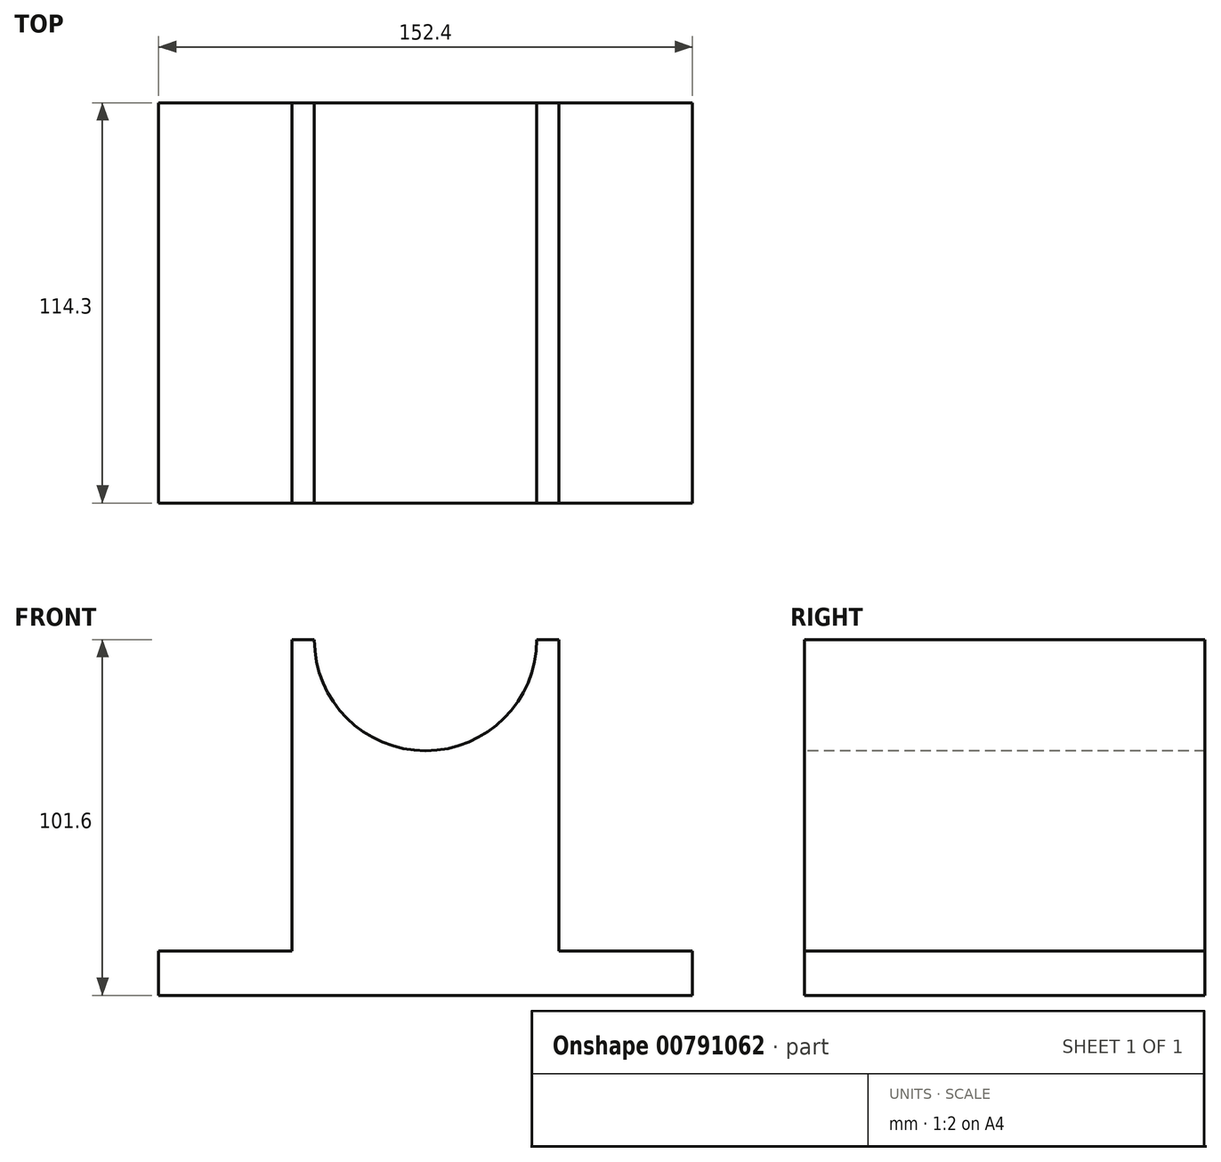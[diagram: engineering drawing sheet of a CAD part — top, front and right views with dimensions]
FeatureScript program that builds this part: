
annotation { "Feature Type Name" : "Feature", "Feature Type Description" : "" }
export const myFeature = defineFeature(function(context is Context, id is Id, definition is map)
    precondition{}
    {
        {
            var Q0;
            Q0=qCreatedBy(makeId("Front.planeOp"),FACE);
            var sketch = newSketch(context, id + "F0", { "sketchPlane" : qUnion([Q0])});
            skLineSegment(sketch, "E0", {"start": v(0, 0) * mm, "end": v(152.4, 0) * mm});
            skLineSegment(sketch, "E1", {"start": v(152.4, 0) * mm, "end": v(152.4, 12.7) * mm});
            skLineSegment(sketch, "E2", {"start": v(152.4, 12.7) * mm, "end": v(114.3, 12.7) * mm});
            skLineSegment(sketch, "E3", {"start": v(114.3, 12.7) * mm, "end": v(114.3, 101.6) * mm});
            skLineSegment(sketch, "E4", {"start": v(114.3, 101.6) * mm, "end": v(38.1, 101.6) * mm});
            skLineSegment(sketch, "E5", {"start": v(38.1, 101.6) * mm, "end": v(38.1, 12.7) * mm});
            skLineSegment(sketch, "E6", {"start": v(38.1, 12.7) * mm, "end": v(0, 12.7) * mm});
            skLineSegment(sketch, "E7", {"start": v(0, 12.7) * mm, "end": v(0, 0) * mm});
            skSolve(sketch);
        }
        {
            var Q0;
            Q0 = qSketchRegion(id + "F0", true);
            extrude(context, id + "F1", {"entities" : qUnion([Q0]), "oppositeDirection" : true, "depth" : 114.3 * mm, "offsetDistance" : 25.4 * mm});
        }
        {
            var Q0;
            Q0=makeQuery(id+"F1.opExtrude","CAP_FACE",FACE,{"disambiguationData":[OSD([sQuery(id+"F0.wireOp",EDGE,"E0"),sQuery(id+"F0.wireOp",EDGE,"E1"),sQuery(id+"F0.wireOp",EDGE,"E2"),sQuery(id+"F0.wireOp",EDGE,"E3"),sQuery(id+"F0.wireOp",EDGE,"E4"),sQuery(id+"F0.wireOp",EDGE,"E5"),sQuery(id+"F0.wireOp",EDGE,"E6"),sQuery(id+"F0.wireOp",EDGE,"E7")])],"isStart":true});
            var sketch = newSketch(context, id + "F2", { "sketchPlane" : qUnion([Q0])});
            skLineSegment(sketch, "E8", {"start": v(38.1, 101.6) * mm, "end": v(44.45, 101.6) * mm, "construction": true});
            skLineSegment(sketch, "E9", {"start": v(44.45, 101.6) * mm, "end": v(107.95, 101.6) * mm, "construction": true});
            skLineSegment(sketch, "E10", {"start": v(107.95, 101.6) * mm, "end": v(114.3, 101.6) * mm, "construction": true});
            skArc(sketch, "E11", {"start": v(44.45, 101.6) * mm, "mid": v(76.2, 69.85) * mm, "end": v(107.95, 101.6) * mm});
            skSolve(sketch);
        }
        {
            var Q0;
            Q0 = qSketchRegion(id + "F2", true);
            var Q1;
            {var subQ0=sQuery(id+"F2.wireOp",EDGE,"E11");Q1=makeQuery(id+"F2.imprint","IMPRINT",FACE,{"disambiguationData":[TD([[makeQuery(id+"F2.imprint","IMPRINT",EDGE,{"derivedFrom":subQ0}),1.0]])]});}
            extrude(context, id + "F3", {"entities" : qUnion([Q0, Q1]), "operationType" : NewBodyOperationType.REMOVE, "oppositeDirection" : true, "depth" : 114.3 * mm, "offsetDistance" : 25.4 * mm});
        }
    });
